# Revit family: TD92_VIR722_AZU070_RVT20_R00
name_source: partatom
category: Mobiliário
units: mm (PartAtom-declared; Revit-internal decimal feet)

## family parameters
Com base no plano de trabalho = Não
Compartilhado = Não
Corte com vazios quando carregada = Não
Número OmniClass = 23.40.20.00
Ponto de cálculo do ambiente = Não
Sempre na vertical = Sim
Título OmniClass = General Furniture and Specialties

## types (1)
- TD92_VIR722_AZU070_RVT20_R00
    Descrição = A versatilidade é uma qualidade evidente no Banco Apoio Tramontina Vira em Polietileno com Porta Copos. É versátil porque tem a utilidade de ser um banco (quando colocada na posição horizontal) ou um apoio (quando colocado na posição vertical). Inclusive, para quando é usada como apoio, já há até o espaço do copo. É demais! Deixa a vida mais prática, a casa mais alegre, o jardim mais próximo e o trabalho mais prazeroso. Criados com o conceito de durabilidade, garantimos um produto que você poderá ter por muitos anos em sua casa.
    Elevação padrão = 0  [stored 0 ft]
    Fabricante = Tramontina Delta S/A
    Modelo = Banco Apoio Tramontina Vira em Polietileno Azul com Porta Copos
    Nota-chave = 92722070
    URL = https://www.tramontinastore.com

note: [stored X ft] marks values corroborated as IEEE doubles in the binary element streams (Revit-internal decimal feet)
